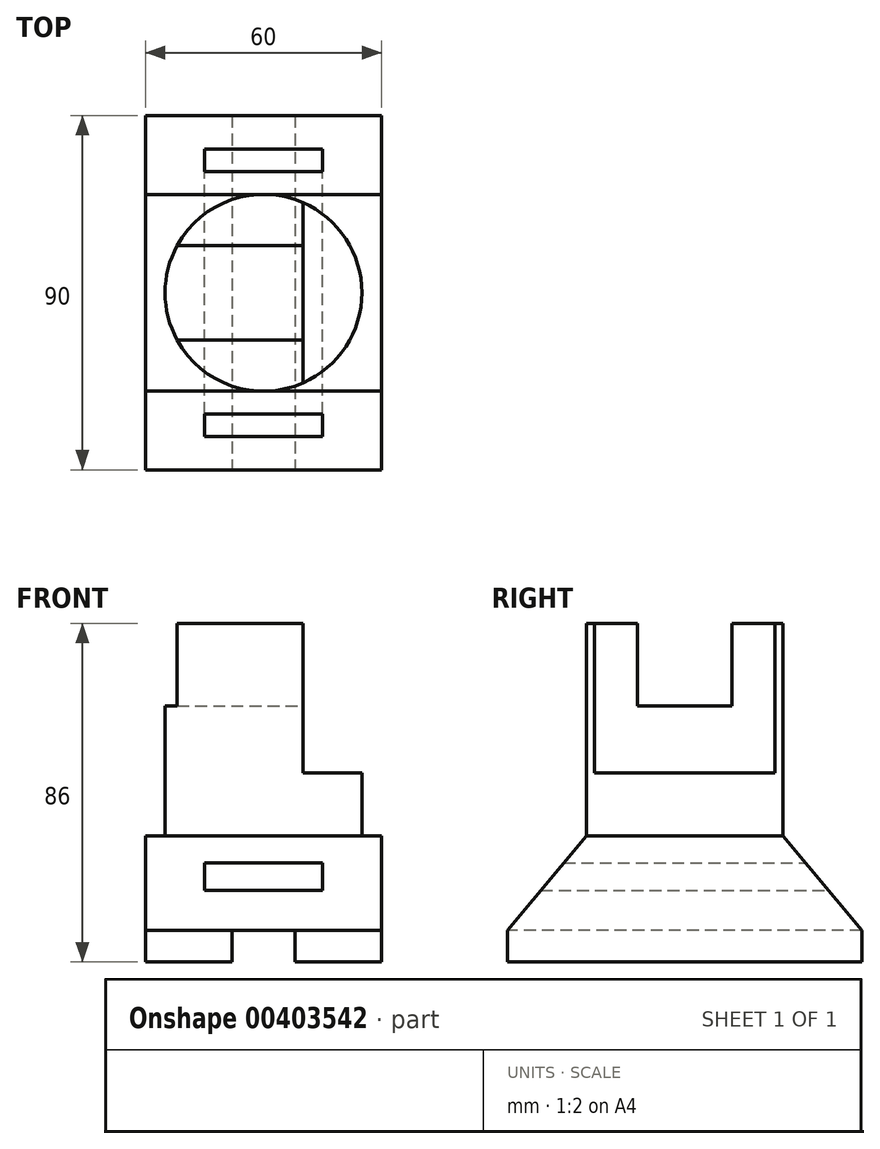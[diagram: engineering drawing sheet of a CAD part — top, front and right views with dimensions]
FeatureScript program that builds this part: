
annotation { "Feature Type Name" : "Feature", "Feature Type Description" : "" }
export const myFeature = defineFeature(function(context is Context, id is Id, definition is map)
    precondition{}
    {
        {
            var Q0;
            Q0=qCreatedBy(makeId("Right.planeOp"),FACE);
            var sketch = newSketch(context, id + "F0", { "sketchPlane" : qUnion([Q0])});
            skLineSegment(sketch, "E0", {"start": v(0, 0) * mm, "end": v(45, 0) * mm});
            skLineSegment(sketch, "E1", {"start": v(45, 0) * mm, "end": v(45, 8) * mm});
            skLineSegment(sketch, "E2", {"start": v(45, 8) * mm, "end": v(25, 32) * mm});
            skLineSegment(sketch, "E3", {"start": v(25, 32) * mm, "end": v(0, 32) * mm});
            skLineSegment(sketch, "E4", {"start": v(0, 32) * mm, "end": v(0, 0) * mm, "construction": true});
            skLineSegment(sketch, "E5.MirrorCS", {"start": v(-25, 32) * mm, "end": v(0, 32) * mm});
            skLineSegment(sketch, "E6.MirrorCS", {"start": v(-45, 8) * mm, "end": v(-25, 32) * mm});
            skLineSegment(sketch, "E7.MirrorCS", {"start": v(-45, 0) * mm, "end": v(-45, 8) * mm});
            skLineSegment(sketch, "E8.MirrorCS", {"start": v(0, 0) * mm, "end": v(-45, 0) * mm});
            skSolve(sketch);
        }
        {
            var Q0;
            Q0 = qSketchRegion(id + "F0", true);
            extrude(context, id + "F1", {"entities" : qUnion([Q0]), "endBound" : BoundingType.SYMMETRIC, "oppositeDirection" : true, "depth" : 60 * mm});
        }
        {
            var Q0;
            Q0=makeQuery(id+"F1.opExtrude","SWEPT_FACE",FACE,{"disambiguationData":[OSD([sQuery(id+"F0.wireOp",EDGE,"E3"),sQuery(id+"F0.wireOp",EDGE,"E5.MirrorCS")])]});
            var sketch = newSketch(context, id + "F2", { "sketchPlane" : qUnion([Q0])});
            skCircle(sketch, "E9", {"center": v(0, 0) * mm, "radius": 25 * mm});
            skPoint(sketch, "E9.centerSnap0", {"position": v(0, -25) * mm});
            skPoint(sketch, "E9.centerSnap1", {"position": v(-30, 0) * mm});
            skSolve(sketch);
        }
        {
            var Q0;
            Q0 = qSketchRegion(id + "F2", true);
            extrude(context, id + "F3", {"entities" : qUnion([Q0]), "operationType" : NewBodyOperationType.ADD, "depth" : 54 * mm});
        }
        {
            var Q0;
            Q0=makeQuery(id+"F3.opExtrude","CAP_FACE",FACE,{"disambiguationData":[OSD([sQuery(id+"F2.wireOp",EDGE,"E9")])],"isStart":false});
            var sketch = newSketch(context, id + "F4", { "sketchPlane" : qUnion([Q0])});
            skLineSegment(sketch, "E10.bottom", {"start": v(-25, -12) * mm, "end": v(25, -12) * mm});
            skLineSegment(sketch, "E10.top", {"start": v(-25, 12) * mm, "end": v(25, 12) * mm});
            skLineSegment(sketch, "E10.left", {"start": v(-25, -12) * mm, "end": v(-25, 12) * mm});
            skLineSegment(sketch, "E10.right", {"start": v(25, -12) * mm, "end": v(25, 12) * mm});
            skPoint(sketch, "E10.middle", {"position": v(0, 0) * mm});
            skSolve(sketch);
        }
        {
            var Q0;
            Q0 = qSketchRegion(id + "F4", true);
            extrude(context, id + "F5", {"entities" : qUnion([Q0]), "operationType" : NewBodyOperationType.REMOVE, "oppositeDirection" : true, "depth" : 21 * mm});
        }
        {
            var Q0;
            {var subQ0=sQuery(id+"F2.wireOp",EDGE,"E9");Q0=makeQuery(id+"F5.boolean.opBoolean","SPLIT",FACE,{"disambiguationData":[TD([makeQuery(id+"F5.opExtrude","SWEPT_FACE",FACE,{"disambiguationData":[OSD([sQuery(id+"F4.wireOp",EDGE,"E10.bottom")])]})])],"derivedFrom":makeQuery(id+"F3.opExtrude","CAP_FACE",FACE,{"disambiguationData":[OSD([subQ0])],"isStart":false})});}
            var sketch = newSketch(context, id + "F6", { "sketchPlane" : qUnion([Q0])});
            skLineSegment(sketch, "E11.bottom", {"start": v(10, 25) * mm, "end": v(35, 25) * mm});
            skLineSegment(sketch, "E11.top", {"start": v(10, -25) * mm, "end": v(35, -25) * mm});
            skLineSegment(sketch, "E11.left", {"start": v(10, 25) * mm, "end": v(10, -25) * mm});
            skLineSegment(sketch, "E11.right", {"start": v(35, 25) * mm, "end": v(35, -25) * mm});
            skSolve(sketch);
        }
        {
            var Q0;
            Q0 = qSketchRegion(id + "F6", true);
            extrude(context, id + "F7", {"entities" : qUnion([Q0]), "operationType" : NewBodyOperationType.REMOVE, "oppositeDirection" : true, "depth" : 38 * mm});
        }
        {
            var Q0;
            Q0=makeQuery(id+"F1.opExtrude","SWEPT_FACE",FACE,{"disambiguationData":[OSD([sQuery(id+"F0.wireOp",EDGE,"E6.MirrorCS")])]});
            var sketch = newSketch(context, id + "F8", { "sketchPlane" : qUnion([Q0])});
            skLineSegment(sketch, "E12.bottom", {"start": v(-15, -0.42) * mm, "end": v(15, -0.42) * mm});
            skLineSegment(sketch, "E12.top", {"start": v(-15, -9.42) * mm, "end": v(15, -9.42) * mm});
            skLineSegment(sketch, "E12.left", {"start": v(-15, -0.42) * mm, "end": v(-15, -9.42) * mm});
            skLineSegment(sketch, "E12.right", {"start": v(15, -0.42) * mm, "end": v(15, -9.42) * mm});
            skSolve(sketch);
        }
        {
            var Q0;
            Q0=makeQuery(id+"F1.opExtrude","CAP_FACE",FACE,{"disambiguationData":[OSD([sQuery(id+"F0.wireOp",EDGE,"E0"),sQuery(id+"F0.wireOp",EDGE,"E1"),sQuery(id+"F0.wireOp",EDGE,"E2"),sQuery(id+"F0.wireOp",EDGE,"E3"),sQuery(id+"F0.wireOp",EDGE,"E5.MirrorCS"),sQuery(id+"F0.wireOp",EDGE,"E6.MirrorCS"),sQuery(id+"F0.wireOp",EDGE,"E7.MirrorCS"),sQuery(id+"F0.wireOp",EDGE,"E8.MirrorCS")])],"isStart":true});
            var sketch = newSketch(context, id + "F9", { "sketchPlane" : qUnion([Q0])});
            skLineSegment(sketch, "E13", {"start": v(-35, 20) * mm, "end": v(51.16, 20) * mm});
            skPoint(sketch, "E13.endSnap0", {"position": v(35, 20) * mm});
            skSolve(sketch);
        }
        {
            var Q0;
            Q0 = qSketchRegion(id + "F8", true);
            var Q1;
            Q1 = qConstructionFilter(qBodyType(qCreatedBy(id + "F9" ,EDGE), BodyType.WIRE), ConstructionObject.NO);
            sweep(context, id + "F10", {"operationType" : NewBodyOperationType.REMOVE, "profiles" : qUnion([Q0]), "path" : qUnion([Q1]), "keepProfileOrientation" : true});
        }
        {
            var Q0;
            Q0=makeQuery(id+"F1.opExtrude","SWEPT_FACE",FACE,{"disambiguationData":[OSD([sQuery(id+"F0.wireOp",EDGE,"E7.MirrorCS")])]});
            var sketch = newSketch(context, id + "F11", { "sketchPlane" : qUnion([Q0])});
            skLineSegment(sketch, "E14.bottom", {"start": v(-8, 8) * mm, "end": v(8, 8) * mm});
            skLineSegment(sketch, "E14.top", {"start": v(-8, 0) * mm, "end": v(8, 0) * mm});
            skLineSegment(sketch, "E14.left", {"start": v(-8, 8) * mm, "end": v(-8, 0) * mm});
            skLineSegment(sketch, "E14.right", {"start": v(8, 8) * mm, "end": v(8, 0) * mm});
            skSolve(sketch);
        }
        {
            var Q0;
            Q0 = qSketchRegion(id + "F11", true);
            extrude(context, id + "F12", {"entities" : qUnion([Q0]), "operationType" : NewBodyOperationType.REMOVE, "endBound" : BoundingType.THROUGH_ALL, "oppositeDirection" : true, "depth" : 25 * mm});
        }
    });
